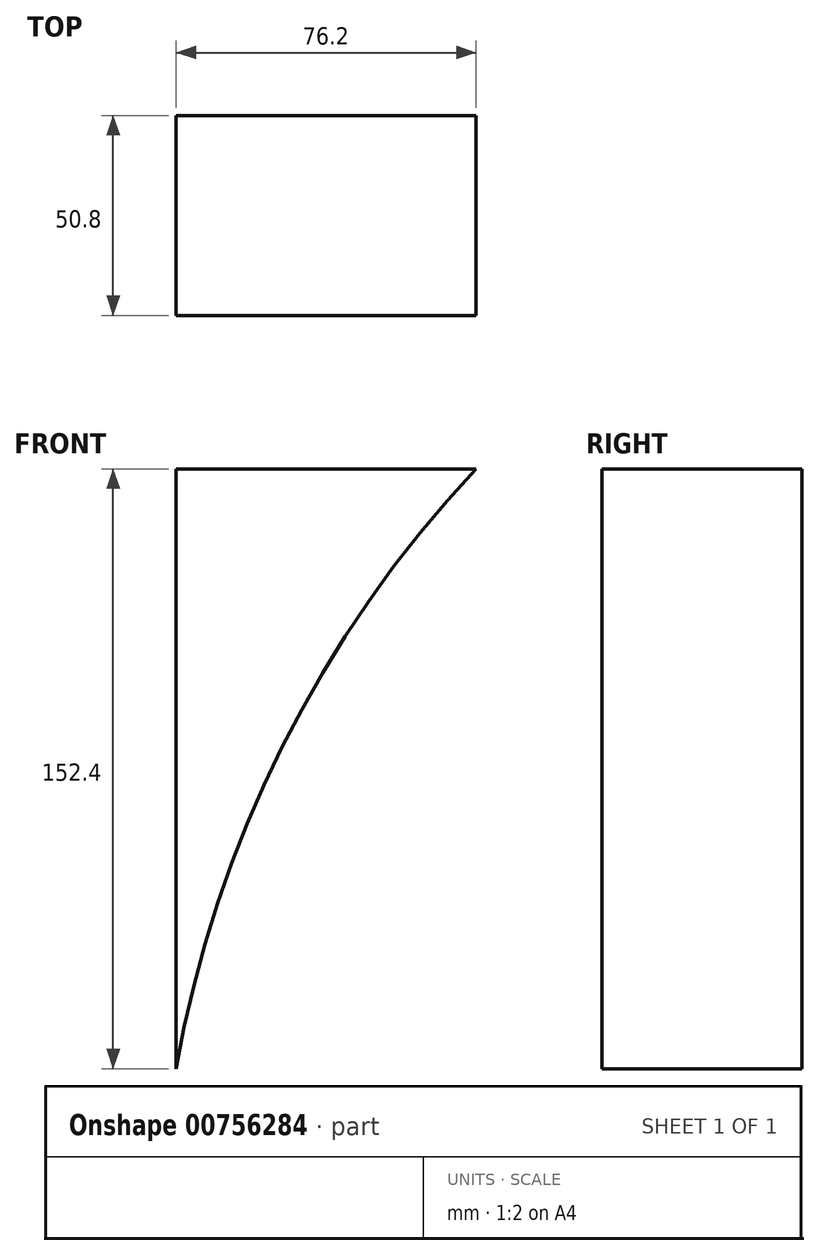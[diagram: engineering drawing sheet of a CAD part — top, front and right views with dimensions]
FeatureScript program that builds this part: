
annotation { "Feature Type Name" : "Feature", "Feature Type Description" : "" }
export const myFeature = defineFeature(function(context is Context, id is Id, definition is map)
    precondition{}
    {
        {
            var Q0;
            Q0=qCreatedBy(makeId("Front.planeOp"),FACE);
            var sketch = newSketch(context, id + "F0", { "sketchPlane" : qUnion([Q0])});
            skLineSegment(sketch, "E0", {"start": v(0, 0) * mm, "end": v(76.2, 0) * mm});
            skLineSegment(sketch, "E1", {"start": v(0, 0) * mm, "end": v(0, -152.4) * mm});
            skArc(sketch, "E2", {"start": v(76.2, 0) * mm, "mid": v(26.94, -70.62) * mm, "end": v(0, -152.4) * mm});
            skSolve(sketch);
        }
        {
            var Q0;
            Q0=makeQuery(id+"F0.imprint","IMPRINT",FACE,{"disambiguationData":[TD([[makeQuery(id+"F0.imprint","IMPRINT",EDGE,{"derivedFrom":sQuery(id+"F0.wireOp",EDGE,"E0")}),-1.0]])]});
            extrude(context, id + "F1", {"entities" : qUnion([Q0]), "depth" : 50.8 * mm, "offsetDistance" : 25.4 * mm});
        }
    });
